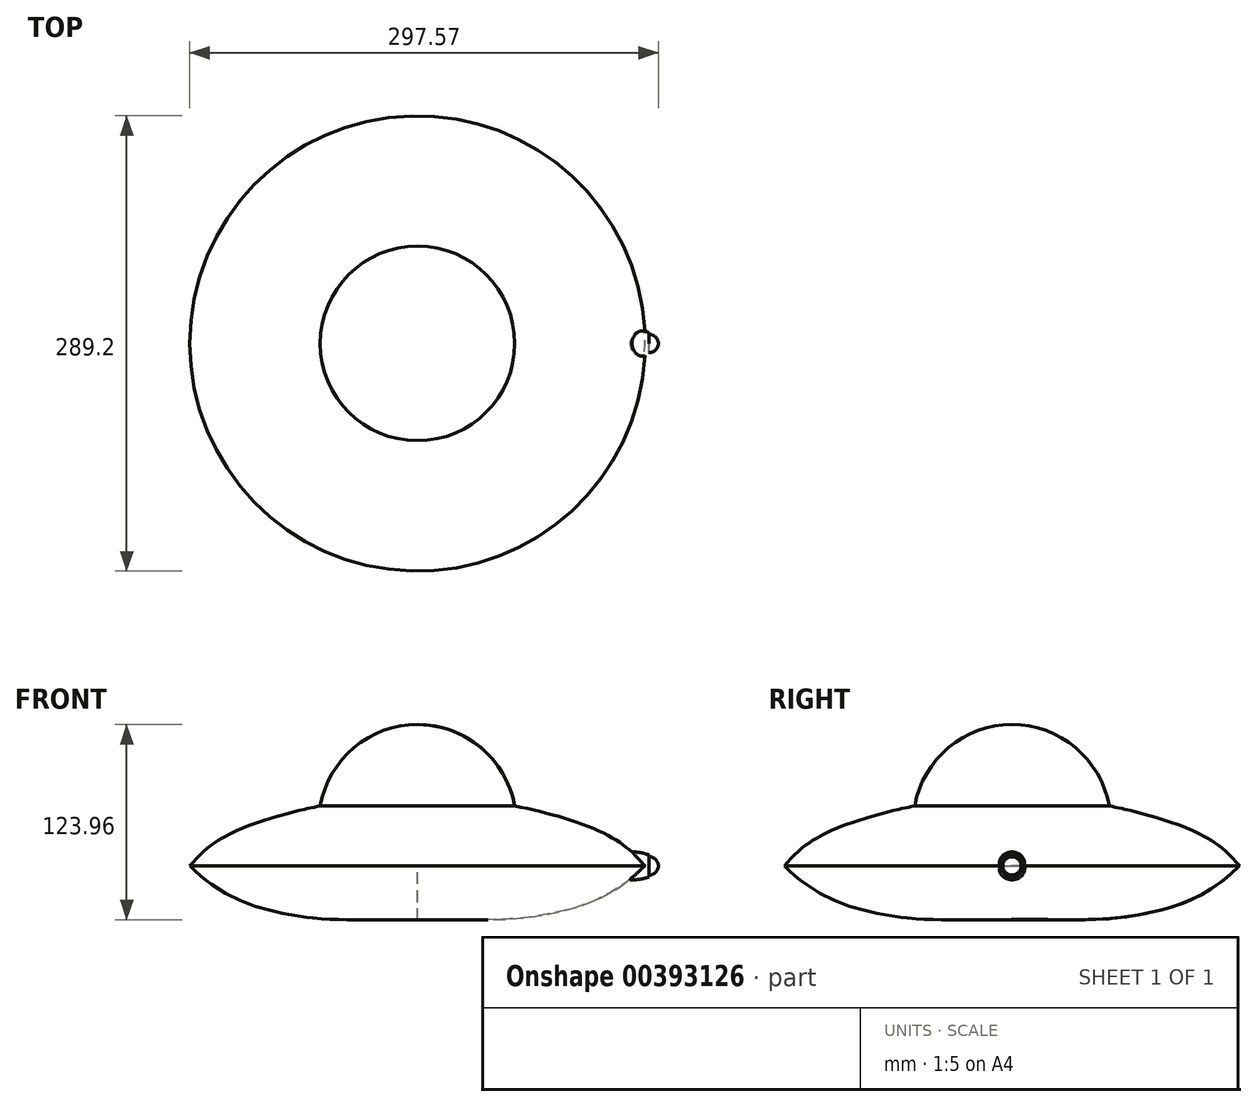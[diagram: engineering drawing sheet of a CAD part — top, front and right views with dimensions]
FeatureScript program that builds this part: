
annotation { "Feature Type Name" : "Feature", "Feature Type Description" : "" }
export const myFeature = defineFeature(function(context is Context, id is Id, definition is map)
    precondition{}
    {
        {
            var Q0;
            Q0=qCreatedBy(makeId("Front.planeOp"),FACE);
            var sketch = newSketch(context, id + "F0", { "sketchPlane" : qUnion([Q0])});
            skFitSpline(sketch, "E0", {"points": [v(0, 42.53) * mm, v(51.24, 39.83) * mm, v(122.4, 18.67) * mm, v(144.6, 0) * mm], "startDerivative": vector(138.93, 1.3) * mm, "endDerivative": vector(67.5, -75.34) * mm});
            skLineSegment(sketch, "E1", {"start": v(0, 42.53) * mm, "end": v(0, 0) * mm});
            skLineSegment(sketch, "E2", {"start": v(0, 0) * mm, "end": v(144.6, 0) * mm});
            skSolve(sketch);
        }
        {
            var Q0;
            Q0=qCreatedBy(makeId("Top.planeOp"),FACE);
            var sketch = newSketch(context, id + "F1", { "sketchPlane" : qUnion([Q0])});
            skEllipticalArc(sketch, "E3", {});
            skLineSegment(sketch, "E4", {"start": v(121.48, 0) * mm, "end": v(152.97, 0) * mm});
            skLineSegment(sketch, "E5", {"start": v(147.12, 6.84) * mm, "end": v(147.12, 6.84) * mm});
            skLineSegment(sketch, "E6", {"start": v(147.12, 6.84) * mm, "end": v(147.12, 5.85) * mm});
            skArc(sketch, "E7", {"start": v(152.97, 0) * mm, "mid": v(151.26, 4.14) * mm, "end": v(147.12, 5.85) * mm});
            const initialGuessF1  = {"E3": [0.13722566794604063, 0, 1, 0, 0.015747293829917908, 0.008799662978141018, 0.8912168780511244, 3.141592653589793]};
            skSetInitialGuess(sketch, initialGuessF1);
            skSolve(sketch);
        }
        {
            var Q0;
            Q0=makeQuery(id+"F1.imprint","IMPRINT",FACE,{"disambiguationData":[TD([[makeQuery(id+"F1.imprint","IMPRINT",EDGE,{"derivedFrom":sQuery(id+"F1.wireOp",EDGE,"E3")}),1.0]])]});
            var Q1;
            Q1=sQuery(id+"F1.wireOp",EDGE,"E4");
            revolve(context, id + "F2", {"entities" : qUnion([Q0]), "axis" : qUnion([Q1]), "revolveType" : RevolveType.FULL});
        }
        {
            var Q0;
            Q0=makeQuery(id+"F0.imprint","IMPRINT",FACE,{"disambiguationData":[TD([[makeQuery(id+"F0.imprint","IMPRINT",EDGE,{"derivedFrom":sQuery(id+"F0.wireOp",EDGE,"E0")}),-1.0]])]});
            var Q1;
            Q1=sQuery(id+"F0.wireOp",EDGE,"E1");
            revolve(context, id + "F3", {"operationType" : NewBodyOperationType.ADD, "entities" : qUnion([Q0]), "axis" : qUnion([Q1]), "revolveType" : RevolveType.FULL});
        }
        {
            var Q0;
            Q0=qCreatedBy(makeId("Front.planeOp"),FACE);
            var sketch = newSketch(context, id + "F4", { "sketchPlane" : qUnion([Q0])});
            skArc(sketch, "E8", {"start": v(62.75, 27.02) * mm, "mid": v(44.37, 71.39) * mm, "end": v(0, 89.77) * mm});
            skLineSegment(sketch, "E9", {"start": v(0, 27.02) * mm, "end": v(0, 89.77) * mm});
            skLineSegment(sketch, "E10", {"start": v(0, 27.02) * mm, "end": v(62.75, 27.02) * mm});
            skSolve(sketch);
        }
        {
            var Q0;
            Q0=makeQuery(id+"F4.imprint","IMPRINT",FACE,{"disambiguationData":[TD([[makeQuery(id+"F4.imprint","IMPRINT",EDGE,{"derivedFrom":sQuery(id+"F4.wireOp",EDGE,"E8")}),1.0]])]});
            var Q1;
            Q1=sQuery(id+"F4.wireOp",EDGE,"E9");
            revolve(context, id + "F5", {"operationType" : NewBodyOperationType.ADD, "entities" : qUnion([Q0]), "axis" : qUnion([Q1]), "revolveType" : RevolveType.FULL});
        }
        {
            var Q0;
            Q0=qCreatedBy(makeId("Right.planeOp"),FACE);
            var sketch = newSketch(context, id + "F6", { "sketchPlane" : qUnion([Q0])});
            skFitSpline(sketch, "E11", {"points": [v(0, -33.79) * mm, v(79.35, -31.23) * mm, v(144.47, 0) * mm], "startDerivative": vector(299.57, -4.8) * mm, "endDerivative": vector(134.66, 138.7) * mm});
            skLineSegment(sketch, "E12", {"start": v(0, -33.79) * mm, "end": v(0, 0) * mm});
            skLineSegment(sketch, "E13", {"start": v(0, 0) * mm, "end": v(144.47, 0) * mm});
            skSolve(sketch);
        }
        {
            var Q0;
            Q0=makeQuery(id+"F6.imprint","IMPRINT",FACE,{"disambiguationData":[TD([[makeQuery(id+"F6.imprint","IMPRINT",EDGE,{"derivedFrom":sQuery(id+"F6.wireOp",EDGE,"E11")}),1.0]])]});
            var Q1;
            Q1=sQuery(id+"F6.wireOp",EDGE,"E12");
            revolve(context, id + "F7", {"entities" : qUnion([Q0]), "axis" : qUnion([Q1]), "revolveType" : RevolveType.FULL});
        }
    });
